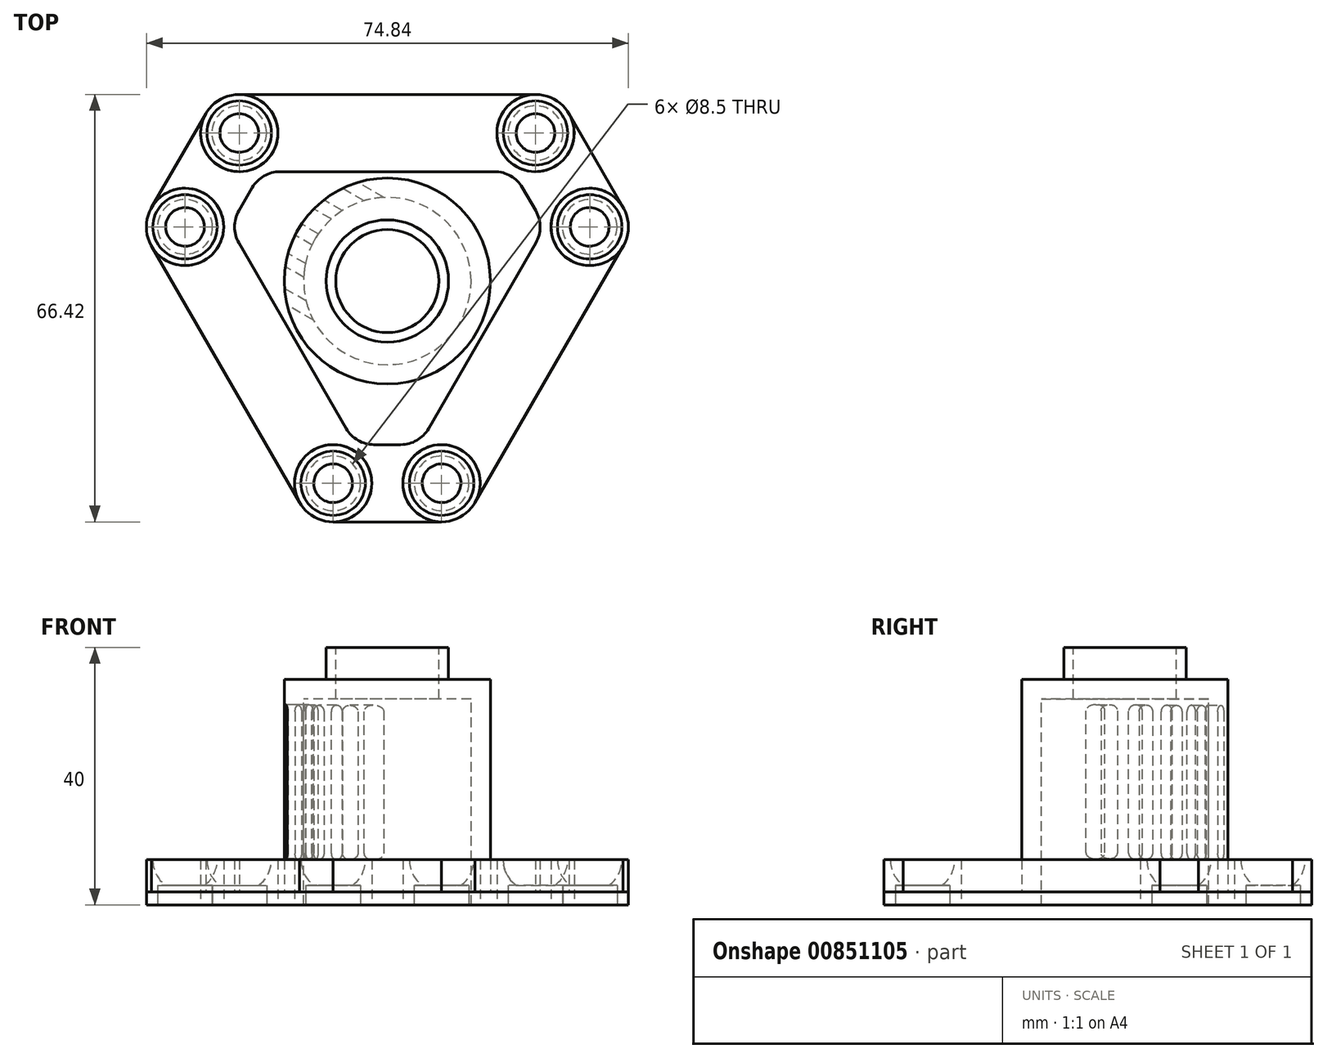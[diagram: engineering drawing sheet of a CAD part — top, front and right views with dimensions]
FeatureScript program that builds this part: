
annotation { "Feature Type Name" : "Feature", "Feature Type Description" : "" }
export const myFeature = defineFeature(function(context is Context, id is Id, definition is map)
    precondition{}
    {
        {
            var Q0;
            Q0=qCreatedBy(makeId("Top.planeOp"),FACE);
            var sketch = newSketch(context, id + "F0", { "sketchPlane" : qUnion([Q0])});
            skCircle(sketch, "E0", {"center": v(-23, 23) * mm, "radius": 6 * mm});
            skSolve(sketch);
        }
        {
            var Q0;
            Q0 = qSketchRegion(id + "F0", true);
            extrude(context, id + "F1", {"entities" : qUnion([Q0]), "depth" : 7 * mm, "offsetDistance" : 25 * mm});
        }
        {
            var Q0;
            Q0=makeQuery(id+"F1.opExtrude","CAP_FACE",FACE,{"disambiguationData":[OSD([sQuery(id+"F0.wireOp",EDGE,"E0")])],"isStart":false});
            var sketch = newSketch(context, id + "F2", { "sketchPlane" : qUnion([Q0])});
            skCircle(sketch, "E1", {"center": v(-23, 23) * mm, "radius": 5 * mm});
            skSolve(sketch);
        }
        {
            var Q0;
            Q0 = qSketchRegion(id + "F2", true);
            extrude(context, id + "F3", {"entities" : qUnion([Q0]), "operationType" : NewBodyOperationType.REMOVE, "oppositeDirection" : true, "depth" : 5 * mm, "offsetDistance" : 25 * mm});
        }
        {
            var Q0;
            Q0=makeQuery(id+"F3.boolean.opBoolean","COPY",EDGE,{"derivedFrom":makeQuery(id+"F3.opExtrude","CAP_EDGE",EDGE,{"disambiguationData":[OSD([sQuery(id+"F2.wireOp",EDGE,"E1")])],"isStart":false})});
            fillet(context, id + "F4", {"entities" : qUnion([Q0]), "radius" : 5 * mm, "tangentPropagation" : true, "allowEdgeOverflow" : false});
        }
        {
            var Q0;
            Q0=makeQuery(id+"F1.opExtrude","CAP_FACE",FACE,{"disambiguationData":[OSD([sQuery(id+"F0.wireOp",EDGE,"E0")])],"isStart":true});
            var sketch = newSketch(context, id + "F5", { "sketchPlane" : qUnion([Q0])});
            skCircle(sketch, "E2", {"center": v(-23, -23) * mm, "radius": 4.25 * mm});
            skSolve(sketch);
        }
        {
            var Q0;
            Q0 = qSketchRegion(id + "F5", true);
            extrude(context, id + "F6", {"entities" : qUnion([Q0]), "operationType" : NewBodyOperationType.REMOVE, "oppositeDirection" : true, "depth" : 3 * mm, "offsetDistance" : 25 * mm});
        }
        {
            var Q0;
            Q0=makeQuery(id+"F1.opExtrude","SWEPT_BODY",BODY,{"disambiguationData":[OSD([sQuery(id+"F0.wireOp",EDGE,"E0")])]});
            var Q1;
            Q1=qCreatedBy(makeId("Right.planeOp"),FACE);
            mirror(context, id + "F7", {"entities" : qUnion([Q0]), "mirrorPlane" : qUnion([Q1])});
        }
        {
            var Q0;
            Q0=qCreatedBy(makeId("Front.planeOp"),FACE);
            var sketch = newSketch(context, id + "F8", { "sketchPlane" : qUnion([Q0])});
            skLineSegment(sketch, "E3", {"start": v(0, 0) * mm, "end": v(0, 53.15) * mm});
            skSolve(sketch);
        }
        {
            var Q0;
            Q0=makeQuery(id+"F1.opExtrude","SWEPT_BODY",BODY,{"disambiguationData":[OSD([sQuery(id+"F0.wireOp",EDGE,"E0")])]});
            var Q1;
            Q1=makeQuery(id+"F7.opPattern","COPY",BODY,{"derivedFrom":makeQuery(id+"F1.opExtrude","SWEPT_BODY",BODY,{"disambiguationData":[OSD([sQuery(id+"F0.wireOp",EDGE,"E0")])]}),"instanceName":"1"});
            var Q2;
            Q2=sQuery(id+"F8.wireOp",EDGE,"E3");
            circularPattern(context, id + "F9", {"entities" : qUnion([Q0, Q1]), "axis" : qUnion([Q2]), "angle" : 360 * degree, "instanceCount" : 3, "equalSpace" : true});
        }
        {
            var Q0;
            Q0=qCreatedBy(makeId("Top.planeOp"),FACE);
            var sketch = newSketch(context, id + "F10", { "sketchPlane" : qUnion([Q0])});
            skLineSegment(sketch, "E4", {"start": v(23, 29) * mm, "end": v(-23, 29) * mm});
            skLineSegment(sketch, "E5", {"start": v(-28.2, 26) * mm, "end": v(-36.61, 11.42) * mm});
            skLineSegment(sketch, "E6", {"start": v(-36.61, 5.42) * mm, "end": v(-13.61, -34.42) * mm});
            skLineSegment(sketch, "E7", {"start": v(-8.42, -37.42) * mm, "end": v(8.42, -37.42) * mm});
            skLineSegment(sketch, "E8", {"start": v(13.61, -34.42) * mm, "end": v(36.61, 5.42) * mm});
            skLineSegment(sketch, "E9", {"start": v(36.61, 11.42) * mm, "end": v(28.2, 26) * mm});
            skCircle(sketch, "E10", {"center": v(-8.42, -31.42) * mm, "radius": 6 * mm});
            skCircle(sketch, "E11", {"center": v(8.42, -31.42) * mm, "radius": 6 * mm});
            skCircle(sketch, "E12", {"center": v(31.42, 8.42) * mm, "radius": 6 * mm});
            skCircle(sketch, "E13", {"center": v(23, 23) * mm, "radius": 6 * mm});
            skCircle(sketch, "E14", {"center": v(-23, 23) * mm, "radius": 6 * mm});
            skCircle(sketch, "E15", {"center": v(-31.42, 8.42) * mm, "radius": 6 * mm});
            skCircle(sketch, "E16", {"center": v(8.42, -31.42) * mm, "radius": 4.25 * mm});
            skCircle(sketch, "E17", {"center": v(-8.42, -31.42) * mm, "radius": 4.25 * mm});
            skCircle(sketch, "E18", {"center": v(31.42, 8.42) * mm, "radius": 4.25 * mm});
            skCircle(sketch, "E19", {"center": v(23, 23) * mm, "radius": 4.25 * mm});
            skCircle(sketch, "E20", {"center": v(-23, 23) * mm, "radius": 4.25 * mm});
            skCircle(sketch, "E21", {"center": v(-31.42, 8.42) * mm, "radius": 4.25 * mm});
            skSolve(sketch);
        }
        {
            var Q0;
            Q0 = qSketchRegion(id + "F10", true);
            extrude(context, id + "F11", {"entities" : qUnion([Q0]), "depth" : 2 * mm, "offsetDistance" : 25 * mm});
        }
        {
            var Q0;
            Q0=makeQuery(id+"F11.opExtrude","CAP_FACE",FACE,{"disambiguationData":[OSD([sQuery(id+"F10.wireOp",EDGE,"E4"),sQuery(id+"F10.wireOp",EDGE,"E5"),sQuery(id+"F10.wireOp",EDGE,"E6"),sQuery(id+"F10.wireOp",EDGE,"E7"),sQuery(id+"F10.wireOp",EDGE,"E8"),sQuery(id+"F10.wireOp",EDGE,"E9"),sQuery(id+"F10.wireOp",EDGE,"E10"),sQuery(id+"F10.wireOp",EDGE,"E11"),sQuery(id+"F10.wireOp",EDGE,"E12"),sQuery(id+"F10.wireOp",EDGE,"E13"),sQuery(id+"F10.wireOp",EDGE,"E14"),sQuery(id+"F10.wireOp",EDGE,"E15"),sQuery(id+"F10.wireOp",EDGE,"E16"),sQuery(id+"F10.wireOp",EDGE,"E17"),sQuery(id+"F10.wireOp",EDGE,"E18"),sQuery(id+"F10.wireOp",EDGE,"E19"),sQuery(id+"F10.wireOp",EDGE,"E20"),sQuery(id+"F10.wireOp",EDGE,"E21")])],"isStart":false});
            var sketch = newSketch(context, id + "F12", { "sketchPlane" : qUnion([Q0])});
            skCircle(sketch, "E22", {"center": v(23, 23) * mm, "radius": 6 * mm});
            skCircle(sketch, "E23", {"center": v(-23, 23) * mm, "radius": 6 * mm});
            skCircle(sketch, "E24", {"center": v(8.42, -31.42) * mm, "radius": 6 * mm});
            skCircle(sketch, "E25", {"center": v(-8.42, -31.42) * mm, "radius": 6 * mm});
            skCircle(sketch, "E26", {"center": v(-31.42, 8.42) * mm, "radius": 6 * mm});
            skCircle(sketch, "E27", {"center": v(31.42, 8.42) * mm, "radius": 6 * mm});
            skLineSegment(sketch, "E28", {"start": v(23, 29) * mm, "end": v(-23, 29) * mm});
            skLineSegment(sketch, "E29", {"start": v(16.65, 17) * mm, "end": v(-16.65, 17) * mm});
            skLineSegment(sketch, "E30", {"start": v(-20.98, 14.5) * mm, "end": v(-23.05, 10.92) * mm});
            skLineSegment(sketch, "E31", {"start": v(-23.05, 5.92) * mm, "end": v(-6.4, -22.92) * mm});
            skLineSegment(sketch, "E32", {"start": v(-36.61, 11.42) * mm, "end": v(-28.2, 26) * mm});
            skLineSegment(sketch, "E33", {"start": v(-36.61, 5.42) * mm, "end": v(-13.61, -34.42) * mm});
            skLineSegment(sketch, "E34", {"start": v(-8.42, -37.42) * mm, "end": v(8.42, -37.42) * mm});
            skLineSegment(sketch, "E35", {"start": v(13.61, -34.42) * mm, "end": v(36.61, 5.42) * mm});
            skLineSegment(sketch, "E36", {"start": v(36.61, 11.42) * mm, "end": v(28.2, 26) * mm});
            skLineSegment(sketch, "E37", {"start": v(20.98, 14.5) * mm, "end": v(23.05, 10.92) * mm});
            skLineSegment(sketch, "E38", {"start": v(23.05, 5.92) * mm, "end": v(6.4, -22.92) * mm});
            skLineSegment(sketch, "E39", {"start": v(2.07, -25.42) * mm, "end": v(-2.07, -25.42) * mm});
            skPoint(sketch, "E40.visualSharp", {"position": v(19.54, 17) * mm});
            skArc(sketch, "E40.filletArc", {"start": v(20.98, 14.5) * mm, "mid": v(19.15, 16.33) * mm, "end": v(16.65, 17) * mm});
            skPoint(sketch, "E41.visualSharp", {"position": v(24.5, 8.42) * mm});
            skArc(sketch, "E41.filletArc", {"start": v(23.05, 5.92) * mm, "mid": v(23.72, 8.42) * mm, "end": v(23.05, 10.92) * mm});
            skPoint(sketch, "E42.visualSharp", {"position": v(4.95, -25.42) * mm});
            skArc(sketch, "E42.filletArc", {"start": v(2.07, -25.42) * mm, "mid": v(4.57, -24.75) * mm, "end": v(6.4, -22.92) * mm});
            skPoint(sketch, "E43.visualSharp", {"position": v(-4.95, -25.42) * mm});
            skArc(sketch, "E43.filletArc", {"start": v(-6.4, -22.92) * mm, "mid": v(-4.57, -24.75) * mm, "end": v(-2.07, -25.42) * mm});
            skPoint(sketch, "E44.visualSharp", {"position": v(-19.54, 17) * mm});
            skArc(sketch, "E44.filletArc", {"start": v(-16.65, 17) * mm, "mid": v(-19.15, 16.33) * mm, "end": v(-20.98, 14.5) * mm});
            skPoint(sketch, "E45.visualSharp", {"position": v(-24.5, 8.42) * mm});
            skArc(sketch, "E45.filletArc", {"start": v(-23.05, 10.92) * mm, "mid": v(-23.72, 8.42) * mm, "end": v(-23.05, 5.92) * mm});
            skSolve(sketch);
        }
        {
            var Q0;
            {var subQ7=sQuery(id+"F12.wireOp",EDGE,"E28");Q0=makeQuery(id+"F12.imprint","IMPRINT",FACE,{"disambiguationData":[TD([[makeQuery(id+"F12.imprint","IMPRINT",EDGE,{"derivedFrom":subQ7}),1.0]])]});}
            extrude(context, id + "F13", {"entities" : qUnion([Q0]), "depth" : 5 * mm, "offsetDistance" : 25 * mm});
        }
        {
            var Q0;
            Q0=makeQuery(id+"F11.opExtrude","CAP_FACE",FACE,{"disambiguationData":[OSD([sQuery(id+"F10.wireOp",EDGE,"E4"),sQuery(id+"F10.wireOp",EDGE,"E5"),sQuery(id+"F10.wireOp",EDGE,"E6"),sQuery(id+"F10.wireOp",EDGE,"E7"),sQuery(id+"F10.wireOp",EDGE,"E8"),sQuery(id+"F10.wireOp",EDGE,"E9"),sQuery(id+"F10.wireOp",EDGE,"E10"),sQuery(id+"F10.wireOp",EDGE,"E11"),sQuery(id+"F10.wireOp",EDGE,"E12"),sQuery(id+"F10.wireOp",EDGE,"E13"),sQuery(id+"F10.wireOp",EDGE,"E14"),sQuery(id+"F10.wireOp",EDGE,"E15"),sQuery(id+"F10.wireOp",EDGE,"E16"),sQuery(id+"F10.wireOp",EDGE,"E17"),sQuery(id+"F10.wireOp",EDGE,"E18"),sQuery(id+"F10.wireOp",EDGE,"E19"),sQuery(id+"F10.wireOp",EDGE,"E20"),sQuery(id+"F10.wireOp",EDGE,"E21")])],"isStart":false});
            var sketch = newSketch(context, id + "F14", { "sketchPlane" : qUnion([Q0])});
            skCircle(sketch, "E46", {"center": v(0, 0) * mm, "radius": 13 * mm});
            skSolve(sketch);
        }
        {
            var Q0;
            Q0 = qSketchRegion(id + "F14", true);
            extrude(context, id + "F15", {"entities" : qUnion([Q0]), "operationType" : NewBodyOperationType.REMOVE, "endBound" : BoundingType.THROUGH_ALL, "oppositeDirection" : true, "depth" : 25 * mm, "offsetDistance" : 25 * mm});
        }
        {
            var Q0;
            Q0=makeQuery(id+"F11.opExtrude","CAP_FACE",FACE,{"disambiguationData":[OSD([sQuery(id+"F10.wireOp",EDGE,"E4"),sQuery(id+"F10.wireOp",EDGE,"E5"),sQuery(id+"F10.wireOp",EDGE,"E6"),sQuery(id+"F10.wireOp",EDGE,"E7"),sQuery(id+"F10.wireOp",EDGE,"E8"),sQuery(id+"F10.wireOp",EDGE,"E9"),sQuery(id+"F10.wireOp",EDGE,"E10"),sQuery(id+"F10.wireOp",EDGE,"E11"),sQuery(id+"F10.wireOp",EDGE,"E12"),sQuery(id+"F10.wireOp",EDGE,"E13"),sQuery(id+"F10.wireOp",EDGE,"E14"),sQuery(id+"F10.wireOp",EDGE,"E15"),sQuery(id+"F10.wireOp",EDGE,"E16"),sQuery(id+"F10.wireOp",EDGE,"E17"),sQuery(id+"F10.wireOp",EDGE,"E18"),sQuery(id+"F10.wireOp",EDGE,"E19"),sQuery(id+"F10.wireOp",EDGE,"E20"),sQuery(id+"F10.wireOp",EDGE,"E21")])],"isStart":false});
            var sketch = newSketch(context, id + "F16", { "sketchPlane" : qUnion([Q0])});
            skCircle(sketch, "E47", {"center": v(0, 0) * mm, "radius": 16 * mm});
            skSolve(sketch);
        }
        {
            var Q0;
            Q0 = qSketchRegion(id + "F16", true);
            extrude(context, id + "F17", {"entities" : qUnion([Q0]), "operationType" : NewBodyOperationType.ADD, "depth" : 30 * mm, "offsetDistance" : 25 * mm});
        }
        {
            var Q0;
            Q0=makeQuery(id+"F17.opExtrude","CAP_FACE",FACE,{"disambiguationData":[OSD([sQuery(id+"F16.wireOp",EDGE,"E47")])],"isStart":true});
            var sketch = newSketch(context, id + "F18", { "sketchPlane" : qUnion([Q0])});
            skCircle(sketch, "E48", {"center": v(0, 0) * mm, "radius": 13 * mm});
            skSolve(sketch);
        }
        {
            var Q0;
            Q0 = qSketchRegion(id + "F18", true);
            extrude(context, id + "F19", {"entities" : qUnion([Q0]), "operationType" : NewBodyOperationType.REMOVE, "endBound" : BoundingType.THROUGH_ALL, "oppositeDirection" : true, "depth" : 25 * mm, "offsetDistance" : 25 * mm});
        }
        {
            var Q0;
            Q0=makeQuery(id+"F17.opExtrude","CAP_FACE",FACE,{"disambiguationData":[OSD([sQuery(id+"F16.wireOp",EDGE,"E47")])],"isStart":false});
            var sketch = newSketch(context, id + "F20", { "sketchPlane" : qUnion([Q0])});
            skCircle(sketch, "E49", {"center": v(0, 0) * mm, "radius": 16 * mm});
            skSolve(sketch);
        }
        {
            var Q0;
            Q0 = qSketchRegion(id + "F20", true);
            extrude(context, id + "F21", {"entities" : qUnion([Q0]), "operationType" : NewBodyOperationType.ADD, "depth" : 3 * mm, "offsetDistance" : 25 * mm});
        }
        {
            var Q0;
            Q0=makeQuery(id+"F21.opExtrude","CAP_FACE",FACE,{"disambiguationData":[OSD([sQuery(id+"F20.wireOp",EDGE,"E49")])],"isStart":false});
            var sketch = newSketch(context, id + "F22", { "sketchPlane" : qUnion([Q0])});
            skCircle(sketch, "E50", {"center": v(0, 0) * mm, "radius": 8 * mm});
            skSolve(sketch);
        }
        {
            var Q0;
            Q0 = qSketchRegion(id + "F22", true);
            extrude(context, id + "F23", {"entities" : qUnion([Q0]), "operationType" : NewBodyOperationType.REMOVE, "oppositeDirection" : true, "depth" : 3 * mm, "offsetDistance" : 25 * mm});
        }
        {
            var Q0;
            Q0=makeQuery(id+"F21.opExtrude","CAP_FACE",FACE,{"disambiguationData":[OSD([sQuery(id+"F20.wireOp",EDGE,"E49")])],"isStart":false});
            var sketch = newSketch(context, id + "F24", { "sketchPlane" : qUnion([Q0])});
            skCircle(sketch, "E51", {"center": v(0, 0) * mm, "radius": 9.5 * mm});
            skCircle(sketch, "E52", {"center": v(0, 0) * mm, "radius": 8 * mm});
            skSolve(sketch);
        }
        {
            var Q0;
            Q0 = qSketchRegion(id + "F24", true);
            extrude(context, id + "F25", {"entities" : qUnion([Q0]), "operationType" : NewBodyOperationType.ADD, "depth" : 5 * mm, "offsetDistance" : 25 * mm});
        }
        {
            var Q0;
            Q0=makeQuery(id+"F13.opExtrude","SWEPT_FACE",FACE,{"disambiguationData":[OSD([sQuery(id+"F12.wireOp",EDGE,"E30")])]});
            cPlane(context, id + "F26", {"entities" : qUnion([Q0]), "cplaneType" : CPlaneType.OFFSET, "offset" : 8 * mm, "width" : 150 * mm, "height" : 150 * mm});
        }
        {
            var Q0;
            Q0=qCreatedBy(id+"F26.planeOp",FACE);
            var sketch = newSketch(context, id + "F27", { "sketchPlane" : qUnion([Q0])});
            skLineSegment(sketch, "E53.left", {"start": v(-1, 8) * mm, "end": v(-1, 30) * mm});
            skLineSegment(sketch, "E53.right", {"start": v(1, 8) * mm, "end": v(1, 30) * mm});
            skPoint(sketch, "E53.middle", {"position": v(0, 19) * mm});
            skArc(sketch, "E54", {"start": v(1, 30) * mm, "mid": v(0, 31) * mm, "end": v(-1, 30) * mm});
            skArc(sketch, "E55", {"start": v(-1, 8) * mm, "mid": v(0, 7) * mm, "end": v(1, 8) * mm});
            skLineSegment(sketch, "E56.1.0.0", {"start": v(4, 8) * mm, "end": v(4, 30) * mm});
            skArc(sketch, "E56.1.0.1", {"start": v(6, 30) * mm, "mid": v(5, 31) * mm, "end": v(4, 30) * mm});
            skLineSegment(sketch, "E56.1.0.2", {"start": v(6, 8) * mm, "end": v(6, 30) * mm});
            skArc(sketch, "E56.1.0.3", {"start": v(4, 8) * mm, "mid": v(5, 7) * mm, "end": v(6, 8) * mm});
            skLineSegment(sketch, "E56.2.0.0", {"start": v(9, 8) * mm, "end": v(9, 30) * mm});
            skArc(sketch, "E56.2.0.1", {"start": v(11, 30) * mm, "mid": v(10, 31) * mm, "end": v(9, 30) * mm});
            skLineSegment(sketch, "E56.2.0.2", {"start": v(11, 8) * mm, "end": v(11, 30) * mm});
            skArc(sketch, "E56.2.0.3", {"start": v(9, 8) * mm, "mid": v(10, 7) * mm, "end": v(11, 8) * mm});
            skLineSegment(sketch, "E56.direction1", {"start": v(-1, 8) * mm, "end": v(4, 8) * mm, "construction": true});
            skLineSegment(sketch, "E57.1.0.0", {"start": v(-6, 8.06) * mm, "end": v(-6, 30.06) * mm});
            skLineSegment(sketch, "E57.1.0.1", {"start": v(-4, 8.06) * mm, "end": v(-4, 30.06) * mm});
            skArc(sketch, "E57.1.0.2", {"start": v(-4, 30.06) * mm, "mid": v(-5, 31.06) * mm, "end": v(-6, 30.06) * mm});
            skArc(sketch, "E57.1.0.3", {"start": v(-6, 8.06) * mm, "mid": v(-5, 7.06) * mm, "end": v(-4, 8.06) * mm});
            skLineSegment(sketch, "E57.2.0.0", {"start": v(-11, 8.12) * mm, "end": v(-11, 30.12) * mm});
            skLineSegment(sketch, "E57.2.0.1", {"start": v(-9, 8.12) * mm, "end": v(-9, 30.12) * mm});
            skArc(sketch, "E57.2.0.2", {"start": v(-9, 30.12) * mm, "mid": v(-10, 31.12) * mm, "end": v(-11, 30.12) * mm});
            skArc(sketch, "E57.2.0.3", {"start": v(-11, 8.12) * mm, "mid": v(-10, 7.12) * mm, "end": v(-9, 8.12) * mm});
            skLineSegment(sketch, "E57.direction1", {"start": v(-1, 8) * mm, "end": v(-6, 8.06) * mm, "construction": true});
            skSolve(sketch);
        }
        {
            var Q0;
            Q0 = qSketchRegion(id + "F27", true);
            var Q1;
            Q1=makeQuery(id+"F19.boolean.opBoolean","MERGE",FACE,{"derivedFrom":[makeQuery(id+"F15.boolean.opBoolean","COPY",FACE,{"derivedFrom":makeQuery(id+"F15.opExtrude","SWEPT_FACE",FACE,{"disambiguationData":[OSD([sQuery(id+"F14.wireOp",EDGE,"E46")])]})}),makeQuery(id+"F19.opExtrude","SWEPT_FACE",FACE,{"disambiguationData":[OSD([sQuery(id+"F18.wireOp",EDGE,"E48")])]})]});
            extrude(context, id + "F28", {"entities" : qUnion([Q0]), "operationType" : NewBodyOperationType.REMOVE, "depth" : 15 * mm, "endBoundEntityFace" : qUnion([Q1]), "offsetDistance" : 25 * mm});
        }
    });
